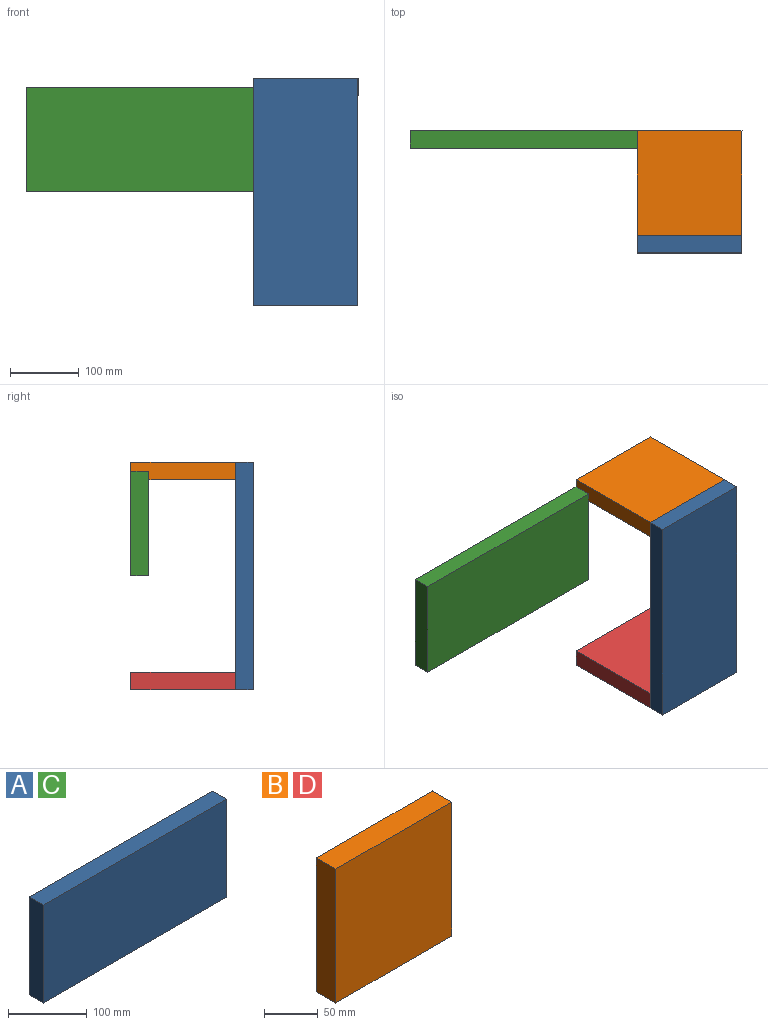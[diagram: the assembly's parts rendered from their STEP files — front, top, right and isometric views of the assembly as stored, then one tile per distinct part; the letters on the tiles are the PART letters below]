
ASSEMBLY  parts=4 mates=3
PART A: 6 faces, bbox 330.2x25.4x152.4 mm
  f0: plane 330.2x25.4mm, normal (0,0,1), area 8387.1mm2, adj f1,f3,f4,f5
  f1: plane 152.4x25.4mm, normal (-1,0,0), area 3871mm2, adj f0,f2,f4,f5
  f2: plane 330.2x25.4mm, normal (0,0,-1), area 8387.1mm2, adj f1,f3,f4,f5
  f3: plane 152.4x25.4mm, normal (1,0,0), area 3871mm2, adj f0,f2,f4,f5
  f4: plane 330.2x152.4mm, normal (0,-1,0), area 50322.5mm2, adj f0,f1,f2,f3
  f5: plane 330.2x152.4mm, normal (0,1,0), area 50322.5mm2, adj f0,f1,f2,f3
PART B: 6 faces, bbox 152.4x25.4x152.4 mm
  f0: plane 152.4x25.4mm, normal (-1,0,0), area 3871mm2, adj f1,f3,f4,f5
  f1: plane 152.4x25.4mm, normal (0,0,-1), area 3871mm2, adj f0,f2,f4,f5
  f2: plane 152.4x25.4mm, normal (1,0,0), area 3871mm2, adj f1,f3,f4,f5
  f3: plane 152.4x25.4mm, normal (0,0,1), area 3871mm2, adj f0,f2,f4,f5
  f4: plane 152.4x152.4mm, normal (0,-1,0), area 23225.8mm2, adj f0,f1,f2,f3
  f5: plane 152.4x152.4mm, normal (0,1,0), area 23225.8mm2, adj f0,f1,f2,f3
PART C: same geometry as A
PART D: same geometry as B
PLACE A rot(axis=(0,-1,0),90deg) t=(-73.93,11.24,-233.53)mm
PLACE B rot(axis=(0.58,-0.58,-0.58),120deg) t=(-64.23,3.11,-182.21)mm
PLACE C t=(-222.95,163.64,-292.63)mm
PLACE D rot(axis=(0.58,-0.58,-0.58),120deg) t=(-64.23,3.11,-487.01)mm
MATE fastened A.f5 <-> D.f2  axis (0,1,0) through (-171.64,11.24,-512.41)mm
MATE fastened B.f2 <-> A.f5  axis (0,-1,0) through (-171.64,11.24,-194.91)mm
MATE fastened B.f0 <-> C.f5  axis (0,1,0) through (-171.64,163.64,-194.91)mm
